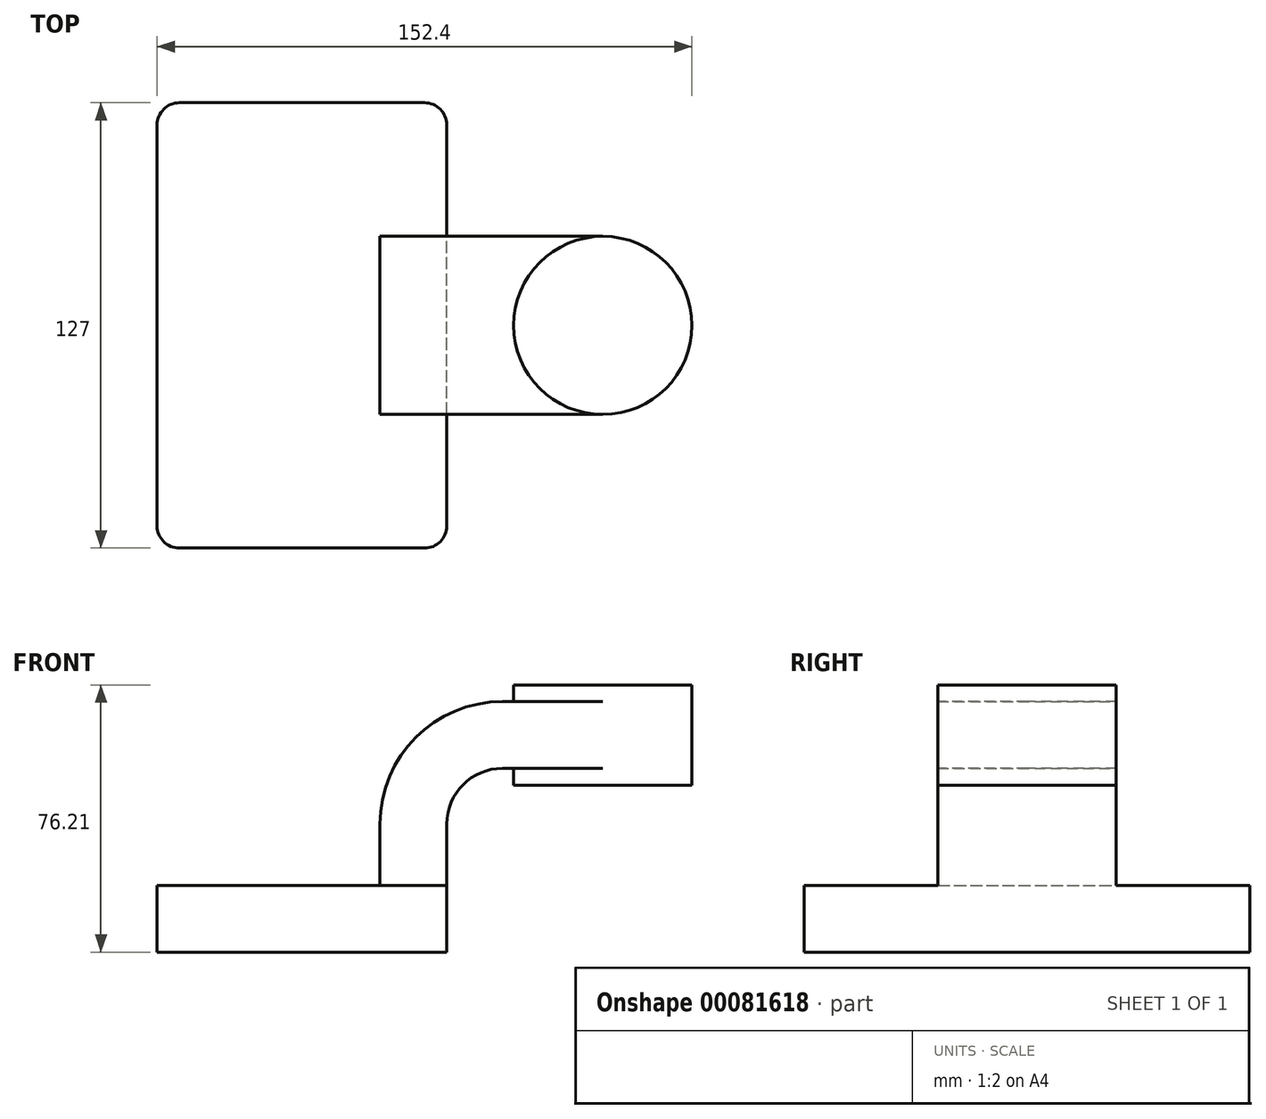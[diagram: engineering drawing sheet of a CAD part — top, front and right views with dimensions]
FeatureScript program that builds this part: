
annotation { "Feature Type Name" : "Feature", "Feature Type Description" : "" }
export const myFeature = defineFeature(function(context is Context, id is Id, definition is map)
    precondition{}
    {
        {
            var Q0;
            Q0=qCreatedBy(makeId("Front.planeOp"),FACE);
            var sketch = newSketch(context, id + "F0", { "sketchPlane" : qUnion([Q0])});
            skLineSegment(sketch, "E0.bottom", {"start": v(-41.28, -9.53) * mm, "end": v(41.28, -9.53) * mm});
            skLineSegment(sketch, "E0.top", {"start": v(-41.28, 9.52) * mm, "end": v(41.27, 9.52) * mm});
            skLineSegment(sketch, "E0.left", {"start": v(-41.27, -9.53) * mm, "end": v(-41.28, 9.52) * mm});
            skLineSegment(sketch, "E0.right", {"start": v(41.28, -9.53) * mm, "end": v(41.27, 9.52) * mm});
            skPoint(sketch, "E0.middle", {"position": v(0, 0) * mm});
            skLineSegment(sketch, "E1.bottom", {"start": v(111.12, 66.67) * mm, "end": v(60.32, 66.67) * mm});
            skLineSegment(sketch, "E1.top", {"start": v(111.12, 38.1) * mm, "end": v(60.32, 38.1) * mm});
            skLineSegment(sketch, "E1.left", {"start": v(111.12, 66.68) * mm, "end": v(111.12, 38.1) * mm});
            skLineSegment(sketch, "E1.right", {"start": v(60.32, 66.67) * mm, "end": v(60.32, 38.1) * mm});
            skPoint(sketch, "E1.middle", {"position": v(85.72, 52.39) * mm});
            skLineSegment(sketch, "E2", {"start": v(41.27, 9.52) * mm, "end": v(41.27, 27) * mm});
            skArc(sketch, "E3", {"start": v(41.27, 27) * mm, "mid": v(45.92, 38.23) * mm, "end": v(57.15, 42.88) * mm});
            skLineSegment(sketch, "E4", {"start": v(57.15, 42.88) * mm, "end": v(85.72, 42.88) * mm});
            skLineSegment(sketch, "E5.0", {"start": v(57.15, 61.93) * mm, "end": v(85.72, 61.93) * mm});
            skArc(sketch, "E5.1", {"start": v(22.23, 27) * mm, "mid": v(32.45, 51.7) * mm, "end": v(57.15, 61.93) * mm});
            skLineSegment(sketch, "E5.2", {"start": v(22.22, 9.52) * mm, "end": v(22.22, 27) * mm});
            skLineSegment(sketch, "E6", {"start": v(85.72, 38.1) * mm, "end": v(85.72, 66.67) * mm});
            skFitSpline(sketch, "E7", {"points": [v(-41.28, 9.53) * mm, v(57.15, 61.93) * mm], "startDerivative": vector(75.68, 102.74) * mm, "endDerivative": vector(156.66, -2.19) * mm});
            skSolve(sketch);
        }
        {
            var Q0;
            Q0=makeQuery(id+"F0.imprint","IMPRINT",FACE,{"disambiguationData":[TD([[makeQuery(id+"F0.imprint","IMPRINT",EDGE,{"derivedFrom":sQuery(id+"F0.wireOp",EDGE,"E0.bottom")}),1.0]])]});
            extrude(context, id + "F1", {"entities" : qUnion([Q0]), "endBound" : BoundingType.SYMMETRIC, "depth" : 127 * mm});
        }
        {
            var Q0;
            {var subQ1=sQuery(id+"F0.wireOp",EDGE,"E2");Q0=makeQuery(id+"F0.imprint","IMPRINT",FACE,{"disambiguationData":[TD([[makeQuery(id+"F0.imprint","IMPRINT",EDGE,{"derivedFrom":subQ1}),1.0]])]});}
            var Q1;
            {var subQ0=sQuery(id+"F0.wireOp",EDGE,"E5.0");var subQ1=sQuery(id+"F0.wireOp",EDGE,"E1.right");var subQ2=makeQuery(id+"F0.imprint","INTERSECT",VERTEX,{"derivedFrom":[subQ1,subQ0]});Q1=makeQuery(id+"F0.imprint","IMPRINT",FACE,{"disambiguationData":[TD([[makeQuery(id+"F0.imprint","IMPRINT",EDGE,{"disambiguationData":[TD([[subQ2,-1.0]])],"derivedFrom":subQ1}),1.0]])]});}
            extrude(context, id + "F2", {"entities" : qUnion([Q0, Q1]), "operationType" : NewBodyOperationType.ADD, "endBound" : BoundingType.SYMMETRIC, "depth" : 50.8 * mm});
        }
        {
            var Q0;
            Q0=makeQuery(id+"F0.imprint","IMPRINT",FACE,{"disambiguationData":[TD([[makeQuery(id+"F0.imprint","IMPRINT",EDGE,{"derivedFrom":sQuery(id+"F0.wireOp",EDGE,"E5.1")}),1.0]])]});
            extrude(context, id + "F3", {"entities" : qUnion([Q0]), "operationType" : NewBodyOperationType.ADD, "endBound" : BoundingType.SYMMETRIC, "depth" : 16.5 * mm});
        }
        {
            var Q0;
            {var subQ0=sQuery(id+"F0.wireOp",EDGE,"E1.left");Q0=makeQuery(id+"F0.imprint","IMPRINT",FACE,{"disambiguationData":[TD([[makeQuery(id+"F0.imprint","IMPRINT",EDGE,{"derivedFrom":subQ0}),-1.0]])]});}
            var Q1;
            Q1=sQuery(id+"F0.wireOp",EDGE,"E6");
            revolve(context, id + "F4", {"operationType" : NewBodyOperationType.ADD, "entities" : qUnion([Q0]), "axis" : qUnion([Q1]), "revolveType" : RevolveType.FULL});
        }
        {
            var Q0;
            Q0=makeQuery(id+"F1.opExtrude","CAP_EDGE",EDGE,{"disambiguationData":[OSD([sQuery(id+"F0.wireOp",EDGE,"E0.left")])],"isStart":false});
            var Q1;
            Q1=makeQuery(id+"F1.opExtrude","CAP_EDGE",EDGE,{"disambiguationData":[OSD([sQuery(id+"F0.wireOp",EDGE,"E0.left")])],"isStart":true});
            var Q2;
            Q2=makeQuery(id+"F1.opExtrude","CAP_EDGE",EDGE,{"disambiguationData":[OSD([sQuery(id+"F0.wireOp",EDGE,"E0.right")])],"isStart":false});
            var Q3;
            Q3=makeQuery(id+"F1.opExtrude","CAP_EDGE",EDGE,{"disambiguationData":[OSD([sQuery(id+"F0.wireOp",EDGE,"E0.right")])],"isStart":true});
            fillet(context, id + "F5", {"entities" : qUnion([Q0, Q1, Q2, Q3]), "radius" : 6.35 * mm, "tangentPropagation" : true, "allowEdgeOverflow" : false});
        }
    });
